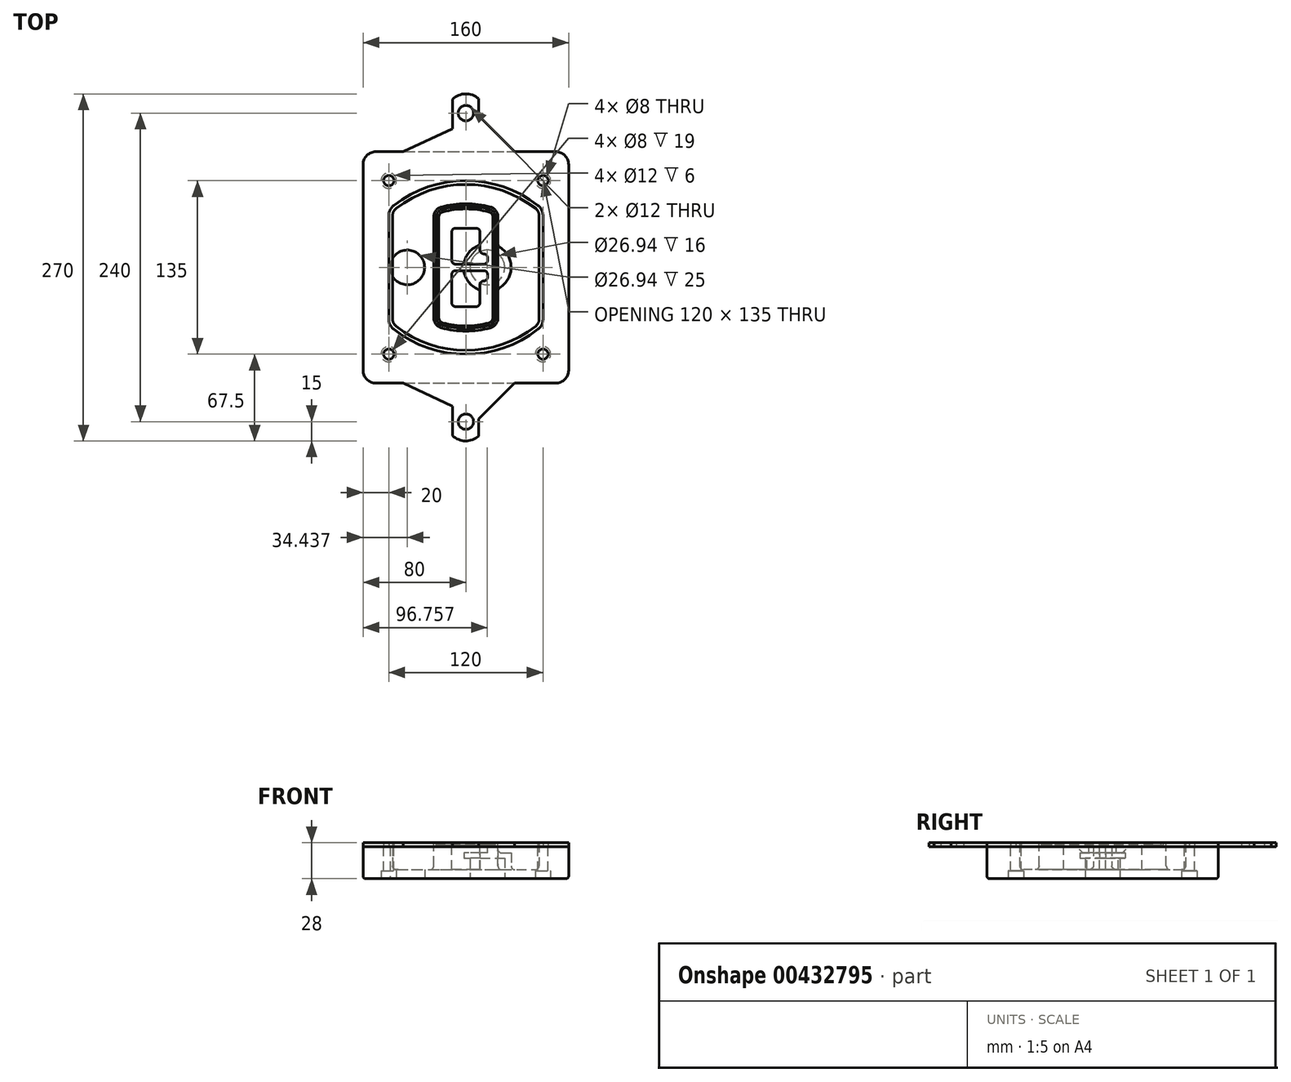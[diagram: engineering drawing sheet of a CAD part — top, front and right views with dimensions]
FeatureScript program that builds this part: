
annotation { "Feature Type Name" : "Feature", "Feature Type Description" : "" }
export const myFeature = defineFeature(function(context is Context, id is Id, definition is map)
    precondition{}
    {
        {
            var Q0;
            Q0=qCreatedBy(makeId("Top.planeOp"),FACE);
            var sketch = newSketch(context, id + "F0", { "sketchPlane" : qUnion([Q0])});
            skPoint(sketch, "E0.rect.middle", {"position": v(0, 0) * mm});
            skLineSegment(sketch, "E1.bottom", {"start": v(-70, -90) * mm, "end": v(70, -90) * mm});
            skLineSegment(sketch, "E1.top", {"start": v(-70, 90) * mm, "end": v(70, 90) * mm});
            skLineSegment(sketch, "E1.left", {"start": v(-80, -80) * mm, "end": v(-80, 80) * mm});
            skLineSegment(sketch, "E1.right", {"start": v(80, -80) * mm, "end": v(80, 80) * mm});
            skLineSegment(sketch, "E2", {"start": v(-80, 90) * mm, "end": v(80, -90) * mm, "construction": true});
            skLineSegment(sketch, "E3", {"start": v(80, 90) * mm, "end": v(-80, -90) * mm, "construction": true});
            skCircle(sketch, "E4", {"center": v(-60, 67.5) * mm, "radius": 4 * mm});
            skCircle(sketch, "E5", {"center": v(60, 67.5) * mm, "radius": 4 * mm});
            skCircle(sketch, "E6", {"center": v(60, -67.5) * mm, "radius": 4 * mm});
            skCircle(sketch, "E7", {"center": v(-60, -67.5) * mm, "radius": 4 * mm});
            skLineSegment(sketch, "E8", {"start": v(-60, 67.5) * mm, "end": v(60, 67.5) * mm, "construction": true});
            skLineSegment(sketch, "E9", {"start": v(60, 67.5) * mm, "end": v(60, -67.5) * mm, "construction": true});
            skLineSegment(sketch, "E10", {"start": v(60, -67.5) * mm, "end": v(-60, -67.5) * mm, "construction": true});
            skLineSegment(sketch, "E11", {"start": v(-60, -67.5) * mm, "end": v(-60, 67.5) * mm, "construction": true});
            skLineSegment(sketch, "E12", {"start": v(-60, 40.3) * mm, "end": v(-60, -40.3) * mm});
            skLineSegment(sketch, "E13", {"start": v(60, 40.3) * mm, "end": v(60, -40.3) * mm});
            skArc(sketch, "E14", {"start": v(56.15, 48.18) * mm, "mid": v(0, 67.5) * mm, "end": v(-56.15, 48.18) * mm});
            skArc(sketch, "E15", {"start": v(-56.15, -48.18) * mm, "mid": v(0, -67.5) * mm, "end": v(56.15, -48.18) * mm});
            skLineSegment(sketch, "E16", {"start": v(-60, 0) * mm, "end": v(60, 0) * mm, "construction": true});
            skPoint(sketch, "E17.visualSharp", {"position": v(-60, -45) * mm});
            skArc(sketch, "E17.filletArc", {"start": v(-60, -40.3) * mm, "mid": v(-58.99, -44.68) * mm, "end": v(-56.15, -48.18) * mm});
            skPoint(sketch, "E18.visualSharp", {"position": v(-60, 45) * mm});
            skArc(sketch, "E18.filletArc", {"start": v(-56.15, 48.18) * mm, "mid": v(-58.99, 44.68) * mm, "end": v(-60, 40.3) * mm});
            skPoint(sketch, "E19.visualSharp", {"position": v(60, 45) * mm});
            skArc(sketch, "E19.filletArc", {"start": v(60, 40.3) * mm, "mid": v(58.99, 44.68) * mm, "end": v(56.15, 48.18) * mm});
            skPoint(sketch, "E20.visualSharp", {"position": v(60, -45) * mm});
            skArc(sketch, "E20.filletArc", {"start": v(56.15, -48.18) * mm, "mid": v(58.99, -44.68) * mm, "end": v(60, -40.3) * mm});
            skPoint(sketch, "E21.visualSharp", {"position": v(-80, 90) * mm});
            skArc(sketch, "E21.filletArc", {"start": v(-70, 90) * mm, "mid": v(-77.07, 87.07) * mm, "end": v(-80, 80) * mm});
            skPoint(sketch, "E22.visualSharp", {"position": v(80, 90) * mm});
            skArc(sketch, "E22.filletArc", {"start": v(80, 80) * mm, "mid": v(77.07, 87.07) * mm, "end": v(70, 90) * mm});
            skPoint(sketch, "E23.visualSharp", {"position": v(80, -90) * mm});
            skArc(sketch, "E23.filletArc", {"start": v(70, -90) * mm, "mid": v(77.07, -87.07) * mm, "end": v(80, -80) * mm});
            skPoint(sketch, "E24.visualSharp", {"position": v(-80, -90) * mm});
            skArc(sketch, "E24.filletArc", {"start": v(-80, -80) * mm, "mid": v(-77.07, -87.07) * mm, "end": v(-70, -90) * mm});
            skArc(sketch, "E25.0", {"start": v(57, 40.3) * mm, "mid": v(56.3, 43.36) * mm, "end": v(54.3, 45.81) * mm});
            skLineSegment(sketch, "E25.1", {"start": v(57, 40.3) * mm, "end": v(57, -40.3) * mm});
            skArc(sketch, "E25.2", {"start": v(54.3, -45.81) * mm, "mid": v(56.3, -43.36) * mm, "end": v(57, -40.3) * mm});
            skArc(sketch, "E25.3", {"start": v(-54.3, -45.81) * mm, "mid": v(0, -64.5) * mm, "end": v(54.3, -45.81) * mm});
            skArc(sketch, "E25.4", {"start": v(-57, -40.3) * mm, "mid": v(-56.3, -43.36) * mm, "end": v(-54.3, -45.81) * mm});
            skArc(sketch, "E25.5", {"start": v(54.3, 45.81) * mm, "mid": v(0, 64.5) * mm, "end": v(-54.3, 45.81) * mm});
            skLineSegment(sketch, "E25.6", {"start": v(-57, 40.3) * mm, "end": v(-57, -40.3) * mm});
            skArc(sketch, "E25.7", {"start": v(-54.3, 45.81) * mm, "mid": v(-56.3, 43.36) * mm, "end": v(-57, 40.3) * mm});
            skArc(sketch, "E26.0", {"start": v(-58.62, 51.33) * mm, "mid": v(-62.58, 46.43) * mm, "end": v(-64, 40.3) * mm});
            skArc(sketch, "E26.1", {"start": v(58.62, 51.33) * mm, "mid": v(0, 71.5) * mm, "end": v(-58.62, 51.33) * mm});
            skArc(sketch, "E26.2", {"start": v(64, 40.3) * mm, "mid": v(62.58, 46.43) * mm, "end": v(58.62, 51.33) * mm});
            skLineSegment(sketch, "E26.3", {"start": v(64, 40.3) * mm, "end": v(64, -40.3) * mm});
            skArc(sketch, "E26.4", {"start": v(58.62, -51.33) * mm, "mid": v(62.58, -46.43) * mm, "end": v(64, -40.3) * mm});
            skLineSegment(sketch, "E26.5", {"start": v(-64, 40.3) * mm, "end": v(-64, -40.3) * mm});
            skArc(sketch, "E26.6", {"start": v(-58.62, -51.33) * mm, "mid": v(0, -71.5) * mm, "end": v(58.62, -51.33) * mm});
            skArc(sketch, "E26.7", {"start": v(-64, -40.3) * mm, "mid": v(-62.58, -46.43) * mm, "end": v(-58.62, -51.33) * mm});
            skSolve(sketch);
        }
        {
            var Q0;
            Q0=makeQuery(id+"F0.imprint","IMPRINT",FACE,{"disambiguationData":[TD([[makeQuery(id+"F0.imprint","IMPRINT",EDGE,{"derivedFrom":sQuery(id+"F0.wireOp",EDGE,"E1.bottom")}),1.0]])]});
            var Q1;
            Q1=makeQuery(id+"F0.imprint","IMPRINT",FACE,{"disambiguationData":[TD([[makeQuery(id+"F0.imprint","IMPRINT",EDGE,{"derivedFrom":sQuery(id+"F0.wireOp",EDGE,"E12")}),1.0]])]});
            var Q2;
            Q2=makeQuery(id+"F0.imprint","IMPRINT",FACE,{"disambiguationData":[TD([[makeQuery(id+"F0.imprint","IMPRINT",EDGE,{"derivedFrom":sQuery(id+"F0.wireOp",EDGE,"E25.0")}),1.0]])]});
            var Q3;
            Q3=makeQuery(id+"F0.imprint","IMPRINT",FACE,{"disambiguationData":[TD([[makeQuery(id+"F0.imprint","IMPRINT",EDGE,{"derivedFrom":sQuery(id+"F0.wireOp",EDGE,"E12")}),-1.0]])]});
            extrude(context, id + "F1", {"entities" : qUnion([Q0, Q1, Q2, Q3]), "oppositeDirection" : true, "depth" : 25 * mm});
        }
        {
            var Q0;
            Q0=makeQuery(id+"F0.imprint","IMPRINT",FACE,{"disambiguationData":[TD([[makeQuery(id+"F0.imprint","IMPRINT",EDGE,{"derivedFrom":sQuery(id+"F0.wireOp",EDGE,"E12")}),1.0]])]});
            extrude(context, id + "F2", {"entities" : qUnion([Q0]), "operationType" : NewBodyOperationType.ADD, "depth" : 3 * mm});
        }
        {
            var Q0;
            Q0=makeQuery(id+"F0.imprint","IMPRINT",FACE,{"disambiguationData":[TD([[makeQuery(id+"F0.imprint","IMPRINT",EDGE,{"derivedFrom":sQuery(id+"F0.wireOp",EDGE,"E25.0")}),1.0]])]});
            extrude(context, id + "F3", {"entities" : qUnion([Q0]), "operationType" : NewBodyOperationType.REMOVE, "oppositeDirection" : true, "depth" : 18 * mm});
        }
        {
            var Q0;
            Q0=makeQuery(id+"F2.opExtrude","CAP_FACE",FACE,{"disambiguationData":[OSD([sQuery(id+"F0.wireOp",EDGE,"E12"),sQuery(id+"F0.wireOp",EDGE,"E13"),sQuery(id+"F0.wireOp",EDGE,"E14"),sQuery(id+"F0.wireOp",EDGE,"E15"),sQuery(id+"F0.wireOp",EDGE,"E17.filletArc"),sQuery(id+"F0.wireOp",EDGE,"E18.filletArc"),sQuery(id+"F0.wireOp",EDGE,"E19.filletArc"),sQuery(id+"F0.wireOp",EDGE,"E20.filletArc"),sQuery(id+"F0.wireOp",EDGE,"E25.0"),sQuery(id+"F0.wireOp",EDGE,"E25.1"),sQuery(id+"F0.wireOp",EDGE,"E25.2"),sQuery(id+"F0.wireOp",EDGE,"E25.3"),sQuery(id+"F0.wireOp",EDGE,"E25.4"),sQuery(id+"F0.wireOp",EDGE,"E25.5"),sQuery(id+"F0.wireOp",EDGE,"E25.6"),sQuery(id+"F0.wireOp",EDGE,"E25.7")])],"isStart":false});
            var sketch = newSketch(context, id + "F4", { "sketchPlane" : qUnion([Q0])});
            skArc(sketch, "E27.0", {"start": v(-19.08, -46.97) * mm, "mid": v(0, -49.5) * mm, "end": v(19.08, -46.97) * mm});
            skArc(sketch, "E28.0", {"start": v(19.08, 46.97) * mm, "mid": v(0, 49.5) * mm, "end": v(-19.08, 46.97) * mm});
            skLineSegment(sketch, "E29", {"start": v(-25, 39.25) * mm, "end": v(-25, -39.25) * mm});
            skLineSegment(sketch, "E30", {"start": v(25, 39.25) * mm, "end": v(25, -39.25) * mm});
            skLineSegment(sketch, "E31", {"start": v(-25, 45.1) * mm, "end": v(25, 45.1) * mm, "construction": true});
            skLineSegment(sketch, "E32", {"start": v(-25, -45.1) * mm, "end": v(25, -45.1) * mm, "construction": true});
            skPoint(sketch, "E33.visualSharp", {"position": v(-25, 45.1) * mm});
            skArc(sketch, "E33.filletArc", {"start": v(-19.08, 46.97) * mm, "mid": v(-23.35, 44.11) * mm, "end": v(-25, 39.25) * mm});
            skPoint(sketch, "E34.visualSharp", {"position": v(25, 45.1) * mm});
            skArc(sketch, "E34.filletArc", {"start": v(25, 39.25) * mm, "mid": v(23.35, 44.11) * mm, "end": v(19.08, 46.97) * mm});
            skPoint(sketch, "E35.visualSharp", {"position": v(25, -45.1) * mm});
            skArc(sketch, "E35.filletArc", {"start": v(19.08, -46.97) * mm, "mid": v(23.35, -44.11) * mm, "end": v(25, -39.25) * mm});
            skPoint(sketch, "E36.visualSharp", {"position": v(-25, -45.1) * mm});
            skArc(sketch, "E36.filletArc", {"start": v(-25, -39.25) * mm, "mid": v(-23.35, -44.11) * mm, "end": v(-19.08, -46.97) * mm});
            skArc(sketch, "E37.0", {"start": v(54.3, 45.81) * mm, "mid": v(0, 64.5) * mm, "end": v(-54.3, 45.81) * mm});
            skArc(sketch, "E37.1", {"start": v(-54.3, 45.81) * mm, "mid": v(-56.3, 43.36) * mm, "end": v(-57, 40.3) * mm});
            skLineSegment(sketch, "E37.2", {"start": v(-57, 40.3) * mm, "end": v(-57, -40.3) * mm});
            skArc(sketch, "E37.3", {"start": v(-57, -40.3) * mm, "mid": v(-56.3, -43.36) * mm, "end": v(-54.3, -45.81) * mm});
            skArc(sketch, "E37.4", {"start": v(-54.3, -45.81) * mm, "mid": v(0, -64.5) * mm, "end": v(54.3, -45.81) * mm});
            skArc(sketch, "E37.5", {"start": v(54.3, -45.81) * mm, "mid": v(56.3, -43.36) * mm, "end": v(57, -40.3) * mm});
            skLineSegment(sketch, "E37.6", {"start": v(57, 40.3) * mm, "end": v(57, -40.3) * mm});
            skArc(sketch, "E37.7", {"start": v(57, 40.3) * mm, "mid": v(56.3, 43.36) * mm, "end": v(54.3, 45.81) * mm});
            skLineSegment(sketch, "E38.0", {"start": v(23, 39.25) * mm, "end": v(23, -39.25) * mm});
            skArc(sketch, "E38.1", {"start": v(18.56, -45.04) * mm, "mid": v(21.76, -42.9) * mm, "end": v(23, -39.25) * mm});
            skArc(sketch, "E38.2", {"start": v(-18.56, -45.04) * mm, "mid": v(0, -47.5) * mm, "end": v(18.56, -45.04) * mm});
            skArc(sketch, "E38.3", {"start": v(-23, -39.25) * mm, "mid": v(-21.76, -42.9) * mm, "end": v(-18.56, -45.04) * mm});
            skLineSegment(sketch, "E38.4", {"start": v(-23, 39.25) * mm, "end": v(-23, -39.25) * mm});
            skArc(sketch, "E38.5", {"start": v(23, 39.25) * mm, "mid": v(21.76, 42.9) * mm, "end": v(18.56, 45.04) * mm});
            skArc(sketch, "E38.6", {"start": v(-18.56, 45.04) * mm, "mid": v(-21.76, 42.9) * mm, "end": v(-23, 39.25) * mm});
            skArc(sketch, "E38.7", {"start": v(18.56, 45.04) * mm, "mid": v(0, 47.5) * mm, "end": v(-18.56, 45.04) * mm});
            skArc(sketch, "E39.0", {"start": v(21, 39.25) * mm, "mid": v(20.18, 41.68) * mm, "end": v(18.04, 43.1) * mm});
            skLineSegment(sketch, "E39.1", {"start": v(21, 39.25) * mm, "end": v(21, -39.25) * mm});
            skArc(sketch, "E39.2", {"start": v(18.04, -43.1) * mm, "mid": v(20.18, -41.68) * mm, "end": v(21, -39.25) * mm});
            skArc(sketch, "E39.3", {"start": v(-18.04, -43.1) * mm, "mid": v(0, -45.5) * mm, "end": v(18.04, -43.1) * mm});
            skArc(sketch, "E39.4", {"start": v(-21, -39.25) * mm, "mid": v(-20.18, -41.68) * mm, "end": v(-18.04, -43.1) * mm});
            skArc(sketch, "E39.5", {"start": v(18.04, 43.1) * mm, "mid": v(0, 45.5) * mm, "end": v(-18.04, 43.1) * mm});
            skLineSegment(sketch, "E39.6", {"start": v(-21, 39.25) * mm, "end": v(-21, -39.25) * mm});
            skArc(sketch, "E39.7", {"start": v(-18.04, 43.1) * mm, "mid": v(-20.18, 41.68) * mm, "end": v(-21, 39.25) * mm});
            skLineSegment(sketch, "E40", {"start": v(-25, 0) * mm, "end": v(25, 0) * mm, "construction": true});
            skLineSegment(sketch, "E41", {"start": v(-11, 5.5) * mm, "end": v(-11, 27.5) * mm});
            skLineSegment(sketch, "E42", {"start": v(-8, 30.5) * mm, "end": v(8, 30.5) * mm});
            skLineSegment(sketch, "E43", {"start": v(11, 27.5) * mm, "end": v(11, 13.5) * mm});
            skLineSegment(sketch, "E44", {"start": v(14, 10.5) * mm, "end": v(14, 10.5) * mm});
            skLineSegment(sketch, "E45", {"start": v(17, 7.5) * mm, "end": v(17, 5.5) * mm});
            skLineSegment(sketch, "E46", {"start": v(14, 2.5) * mm, "end": v(-8, 2.5) * mm});
            skPoint(sketch, "E47.visualSharp", {"position": v(-11, 30.5) * mm});
            skArc(sketch, "E47.filletArc", {"start": v(-8, 30.5) * mm, "mid": v(-10.12, 29.62) * mm, "end": v(-11, 27.5) * mm});
            skPoint(sketch, "E48.visualSharp", {"position": v(11, 30.5) * mm});
            skArc(sketch, "E48.filletArc", {"start": v(11, 27.5) * mm, "mid": v(10.12, 29.62) * mm, "end": v(8, 30.5) * mm});
            skPoint(sketch, "E49.visualSharp", {"position": v(11, 10.5) * mm});
            skArc(sketch, "E49.filletArc", {"start": v(11, 13.5) * mm, "mid": v(11.88, 11.38) * mm, "end": v(14, 10.5) * mm});
            skPoint(sketch, "E50.visualSharp", {"position": v(17, 10.5) * mm});
            skArc(sketch, "E50.filletArc", {"start": v(17, 7.5) * mm, "mid": v(16.12, 9.62) * mm, "end": v(14, 10.5) * mm});
            skPoint(sketch, "E51.visualSharp", {"position": v(17, 2.5) * mm});
            skArc(sketch, "E51.filletArc", {"start": v(14, 2.5) * mm, "mid": v(16.12, 3.38) * mm, "end": v(17, 5.5) * mm});
            skPoint(sketch, "E52.visualSharp", {"position": v(-11, 2.5) * mm});
            skArc(sketch, "E52.filletArc", {"start": v(-11, 5.5) * mm, "mid": v(-10.12, 3.38) * mm, "end": v(-8, 2.5) * mm});
            skLineSegment(sketch, "E53.0.MirrorCS", {"start": v(14, -2.5) * mm, "end": v(-8, -2.5) * mm});
            skArc(sketch, "E54.0.MirrorCS", {"start": v(-11, -5.5) * mm, "mid": v(-10.12, -3.38) * mm, "end": v(-8, -2.5) * mm});
            skLineSegment(sketch, "E55.0.MirrorCS", {"start": v(-11, -5.5) * mm, "end": v(-11, -27.5) * mm});
            skArc(sketch, "E56.0.MirrorCS", {"start": v(-8, -30.5) * mm, "mid": v(-10.12, -29.62) * mm, "end": v(-11, -27.5) * mm});
            skLineSegment(sketch, "E57.0.MirrorCS", {"start": v(-8, -30.5) * mm, "end": v(8, -30.5) * mm});
            skArc(sketch, "E58.0.MirrorCS", {"start": v(11, -27.5) * mm, "mid": v(10.12, -29.62) * mm, "end": v(8, -30.5) * mm});
            skLineSegment(sketch, "E59.0.MirrorCS", {"start": v(11, -27.5) * mm, "end": v(11, -13.5) * mm});
            skArc(sketch, "E60.0.MirrorCS", {"start": v(11, -13.5) * mm, "mid": v(11.88, -11.38) * mm, "end": v(14, -10.5) * mm});
            skArc(sketch, "E61.0.MirrorCS", {"start": v(17, -7.5) * mm, "mid": v(16.12, -9.62) * mm, "end": v(14, -10.5) * mm});
            skLineSegment(sketch, "E62.0.MirrorCS", {"start": v(17, -7.5) * mm, "end": v(17, -5.5) * mm});
            skArc(sketch, "E63.0.MirrorCS", {"start": v(14, -2.5) * mm, "mid": v(16.12, -3.38) * mm, "end": v(17, -5.5) * mm});
            skSolve(sketch);
        }
        {
            var Q0;
            Q0=makeQuery(id+"F4.imprint","IMPRINT",FACE,{"disambiguationData":[TD([[makeQuery(id+"F4.imprint","IMPRINT",EDGE,{"derivedFrom":sQuery(id+"F4.wireOp",EDGE,"E27.0")}),1.0]])]});
            var Q1;
            Q1=makeQuery(id+"F4.imprint","IMPRINT",FACE,{"disambiguationData":[TD([[makeQuery(id+"F4.imprint","IMPRINT",EDGE,{"derivedFrom":sQuery(id+"F4.wireOp",EDGE,"E38.0")}),-1.0]])]});
            var Q2;
            Q2=makeQuery(id+"F4.imprint","IMPRINT",FACE,{"disambiguationData":[TD([[makeQuery(id+"F4.imprint","IMPRINT",EDGE,{"derivedFrom":sQuery(id+"F4.wireOp",EDGE,"E39.0")}),1.0]])]});
            extrude(context, id + "F5", {"entities" : qUnion([Q0, Q1, Q2]), "operationType" : NewBodyOperationType.ADD, "endBound" : BoundingType.UP_TO_NEXT, "oppositeDirection" : true, "depth" : 25 * mm});
        }
        {
            var Q0;
            Q0=makeQuery(id+"F4.imprint","IMPRINT",FACE,{"disambiguationData":[TD([[makeQuery(id+"F4.imprint","IMPRINT",EDGE,{"derivedFrom":sQuery(id+"F4.wireOp",EDGE,"E38.0")}),-1.0]])]});
            extrude(context, id + "F6", {"entities" : qUnion([Q0]), "operationType" : NewBodyOperationType.REMOVE, "oppositeDirection" : true, "depth" : 2 * mm});
        }
        {
            var Q0;
            Q0=makeQuery(id+"F1.opExtrude","CAP_FACE",FACE,{"disambiguationData":[OSD([sQuery(id+"F0.wireOp",EDGE,"E1.bottom"),sQuery(id+"F0.wireOp",EDGE,"E1.top"),sQuery(id+"F0.wireOp",EDGE,"E1.left"),sQuery(id+"F0.wireOp",EDGE,"E1.right"),sQuery(id+"F0.wireOp",EDGE,"E4"),sQuery(id+"F0.wireOp",EDGE,"E5"),sQuery(id+"F0.wireOp",EDGE,"E6"),sQuery(id+"F0.wireOp",EDGE,"E7"),sQuery(id+"F0.wireOp",EDGE,"E21.filletArc"),sQuery(id+"F0.wireOp",EDGE,"E22.filletArc"),sQuery(id+"F0.wireOp",EDGE,"E23.filletArc"),sQuery(id+"F0.wireOp",EDGE,"E24.filletArc")])],"isStart":false});
            var sketch = newSketch(context, id + "F7", { "sketchPlane" : qUnion([Q0])});
            skCircle(sketch, "E64", {"center": v(16.76, 0) * mm, "radius": 13.47 * mm});
            skCircle(sketch, "E65", {"center": v(-45.56, 0) * mm, "radius": 13.47 * mm});
            skLineSegment(sketch, "E66", {"start": v(80, 0) * mm, "end": v(-80, 0) * mm});
            skCircle(sketch, "E67", {"center": v(16.76, 0) * mm, "radius": 18.47 * mm});
            skCircle(sketch, "E68", {"center": v(60, -67.5) * mm, "radius": 6 * mm});
            skCircle(sketch, "E69", {"center": v(-60, -67.5) * mm, "radius": 6 * mm});
            skCircle(sketch, "E70", {"center": v(-60, 67.5) * mm, "radius": 6 * mm});
            skCircle(sketch, "E71", {"center": v(60, 67.5) * mm, "radius": 6 * mm});
            skSolve(sketch);
        }
        {
            var Q0;
            {var subQ1=sQuery(id+"F7.wireOp",EDGE,"E66");var subQ4=sQuery(id+"F7.wireOp",EDGE,"E64");var subQ6=makeQuery(id+"F7.imprint","INTERSECT",VERTEX,{"disambiguationData":[OD(0.0)],"derivedFrom":[subQ4,subQ1]});Q0=makeQuery(id+"F7.imprint","IMPRINT",FACE,{"disambiguationData":[TD([[makeQuery(id+"F7.imprint","IMPRINT",EDGE,{"disambiguationData":[TD([[subQ6,-1.0]])],"derivedFrom":subQ4}),-1.0]])]});}
            var Q1;
            {var subQ0=sQuery(id+"F7.wireOp",EDGE,"E66");var subQ1=sQuery(id+"F7.wireOp",EDGE,"E64");var subQ3=makeQuery(id+"F7.imprint","INTERSECT",VERTEX,{"disambiguationData":[OD(0.0)],"derivedFrom":[subQ1,subQ0]});Q1=makeQuery(id+"F7.imprint","IMPRINT",FACE,{"disambiguationData":[TD([[makeQuery(id+"F7.imprint","IMPRINT",EDGE,{"disambiguationData":[TD([[subQ3,-1.0]])],"derivedFrom":subQ1}),1.0]])]});}
            var Q2;
            {var subQ0=sQuery(id+"F7.wireOp",EDGE,"E66");var subQ1=sQuery(id+"F7.wireOp",EDGE,"E64");var subQ3=makeQuery(id+"F7.imprint","INTERSECT",VERTEX,{"disambiguationData":[OD(0.0)],"derivedFrom":[subQ1,subQ0]});Q2=makeQuery(id+"F7.imprint","IMPRINT",FACE,{"disambiguationData":[TD([[makeQuery(id+"F7.imprint","IMPRINT",EDGE,{"disambiguationData":[TD([[subQ3,1.0]])],"derivedFrom":subQ1}),1.0]])]});}
            var Q3;
            {var subQ1=sQuery(id+"F7.wireOp",EDGE,"E66");var subQ4=sQuery(id+"F7.wireOp",EDGE,"E64");var subQ6=makeQuery(id+"F7.imprint","INTERSECT",VERTEX,{"disambiguationData":[OD(0.0)],"derivedFrom":[subQ4,subQ1]});Q3=makeQuery(id+"F7.imprint","IMPRINT",FACE,{"disambiguationData":[TD([[makeQuery(id+"F7.imprint","IMPRINT",EDGE,{"disambiguationData":[TD([[subQ6,1.0]])],"derivedFrom":subQ4}),-1.0]])]});}
            extrude(context, id + "F8", {"entities" : qUnion([Q0, Q1, Q2, Q3]), "operationType" : NewBodyOperationType.ADD, "oppositeDirection" : true, "depth" : 20 * mm});
        }
        {
            var Q0;
            {var subQ0=sQuery(id+"F7.wireOp",EDGE,"E66");var subQ1=sQuery(id+"F7.wireOp",EDGE,"E64");var subQ3=makeQuery(id+"F7.imprint","INTERSECT",VERTEX,{"disambiguationData":[OD(0.0)],"derivedFrom":[subQ1,subQ0]});Q0=makeQuery(id+"F7.imprint","IMPRINT",FACE,{"disambiguationData":[TD([[makeQuery(id+"F7.imprint","IMPRINT",EDGE,{"disambiguationData":[TD([[subQ3,-1.0]])],"derivedFrom":subQ1}),1.0]])]});}
            var Q1;
            {var subQ0=sQuery(id+"F7.wireOp",EDGE,"E66");var subQ1=sQuery(id+"F7.wireOp",EDGE,"E64");var subQ3=makeQuery(id+"F7.imprint","INTERSECT",VERTEX,{"disambiguationData":[OD(0.0)],"derivedFrom":[subQ1,subQ0]});Q1=makeQuery(id+"F7.imprint","IMPRINT",FACE,{"disambiguationData":[TD([[makeQuery(id+"F7.imprint","IMPRINT",EDGE,{"disambiguationData":[TD([[subQ3,1.0]])],"derivedFrom":subQ1}),1.0]])]});}
            extrude(context, id + "F9", {"entities" : qUnion([Q0, Q1]), "operationType" : NewBodyOperationType.REMOVE, "oppositeDirection" : true, "depth" : 16 * mm});
        }
        {
            var Q0;
            {var subQ0=sQuery(id+"F7.wireOp",EDGE,"E66");var subQ1=sQuery(id+"F7.wireOp",EDGE,"E65");var subQ3=makeQuery(id+"F7.imprint","INTERSECT",VERTEX,{"disambiguationData":[OD(0.0)],"derivedFrom":[subQ1,subQ0]});Q0=makeQuery(id+"F7.imprint","IMPRINT",FACE,{"disambiguationData":[TD([[makeQuery(id+"F7.imprint","IMPRINT",EDGE,{"disambiguationData":[TD([[subQ3,-1.0]])],"derivedFrom":subQ1}),1.0]])]});}
            var Q1;
            {var subQ0=sQuery(id+"F7.wireOp",EDGE,"E66");var subQ1=sQuery(id+"F7.wireOp",EDGE,"E65");var subQ3=makeQuery(id+"F7.imprint","INTERSECT",VERTEX,{"disambiguationData":[OD(0.0)],"derivedFrom":[subQ1,subQ0]});Q1=makeQuery(id+"F7.imprint","IMPRINT",FACE,{"disambiguationData":[TD([[makeQuery(id+"F7.imprint","IMPRINT",EDGE,{"disambiguationData":[TD([[subQ3,1.0]])],"derivedFrom":subQ1}),1.0]])]});}
            extrude(context, id + "F10", {"entities" : qUnion([Q0, Q1]), "operationType" : NewBodyOperationType.REMOVE, "oppositeDirection" : true, "depth" : 25 * mm});
        }
        {
            var Q0;
            Q0=makeQuery(id+"F7.imprint","IMPRINT",FACE,{"disambiguationData":[TD([[makeQuery(id+"F7.imprint","IMPRINT",EDGE,{"derivedFrom":sQuery(id+"F7.wireOp",EDGE,"E68")}),1.0]])]});
            var Q1;
            Q1=makeQuery(id+"F7.imprint","IMPRINT",FACE,{"disambiguationData":[TD([[makeQuery(id+"F7.imprint","IMPRINT",EDGE,{"derivedFrom":makeQuery(id+"F1.opExtrude","CAP_EDGE",EDGE,{"disambiguationData":[OSD([sQuery(id+"F0.wireOp",EDGE,"E5")])],"isStart":false})}),-1.0]])]});
            var Q2;
            Q2=makeQuery(id+"F7.imprint","IMPRINT",FACE,{"disambiguationData":[TD([[makeQuery(id+"F7.imprint","IMPRINT",EDGE,{"derivedFrom":sQuery(id+"F7.wireOp",EDGE,"E69")}),1.0]])]});
            var Q3;
            Q3=makeQuery(id+"F7.imprint","IMPRINT",FACE,{"disambiguationData":[TD([[makeQuery(id+"F7.imprint","IMPRINT",EDGE,{"derivedFrom":makeQuery(id+"F1.opExtrude","CAP_EDGE",EDGE,{"disambiguationData":[OSD([sQuery(id+"F0.wireOp",EDGE,"E4")])],"isStart":false})}),-1.0]])]});
            var Q4;
            Q4=makeQuery(id+"F7.imprint","IMPRINT",FACE,{"disambiguationData":[TD([[makeQuery(id+"F7.imprint","IMPRINT",EDGE,{"derivedFrom":sQuery(id+"F7.wireOp",EDGE,"E70")}),1.0]])]});
            var Q5;
            Q5=makeQuery(id+"F7.imprint","IMPRINT",FACE,{"disambiguationData":[TD([[makeQuery(id+"F7.imprint","IMPRINT",EDGE,{"derivedFrom":makeQuery(id+"F1.opExtrude","CAP_EDGE",EDGE,{"disambiguationData":[OSD([sQuery(id+"F0.wireOp",EDGE,"E7")])],"isStart":false})}),-1.0]])]});
            var Q6;
            Q6=makeQuery(id+"F7.imprint","IMPRINT",FACE,{"disambiguationData":[TD([[makeQuery(id+"F7.imprint","IMPRINT",EDGE,{"derivedFrom":sQuery(id+"F7.wireOp",EDGE,"E71")}),1.0]])]});
            var Q7;
            Q7=makeQuery(id+"F7.imprint","IMPRINT",FACE,{"disambiguationData":[TD([[makeQuery(id+"F7.imprint","IMPRINT",EDGE,{"derivedFrom":makeQuery(id+"F1.opExtrude","CAP_EDGE",EDGE,{"disambiguationData":[OSD([sQuery(id+"F0.wireOp",EDGE,"E6")])],"isStart":false})}),-1.0]])]});
            extrude(context, id + "F11", {"entities" : qUnion([Q0, Q1, Q2, Q3, Q4, Q5, Q6, Q7]), "operationType" : NewBodyOperationType.REMOVE, "oppositeDirection" : true, "depth" : 6 * mm});
        }
        {
            var Q0;
            Q0=makeQuery(id+"F9.boolean.opBoolean","COPY",FACE,{"derivedFrom":makeQuery(id+"F9.opExtrude","CAP_FACE",FACE,{"disambiguationData":[OSD([sQuery(id+"F7.wireOp",EDGE,"E64")])],"isStart":false})});
            var sketch = newSketch(context, id + "F12", { "sketchPlane" : qUnion([Q0])});
            skArc(sketch, "E72.0", {"start": v(11, 17.55) * mm, "mid": v(2.57, 11.82) * mm, "end": v(-1.54, 2.5) * mm});
            skArc(sketch, "E72.1", {"start": v(-1.54, -2.5) * mm, "mid": v(2.57, -11.82) * mm, "end": v(11, -17.55) * mm});
            skLineSegment(sketch, "E73", {"start": v(-1.54, -2.5) * mm, "end": v(14, -2.5) * mm});
            skLineSegment(sketch, "E74.0", {"start": v(14, 2.5) * mm, "end": v(-1.54, 2.5) * mm});
            skArc(sketch, "E74.1", {"start": v(14, 2.5) * mm, "mid": v(16.12, 3.38) * mm, "end": v(17, 5.5) * mm});
            skLineSegment(sketch, "E74.2", {"start": v(17, 7.5) * mm, "end": v(17, 5.5) * mm});
            skArc(sketch, "E74.3", {"start": v(17, 7.5) * mm, "mid": v(16.12, 9.62) * mm, "end": v(14, 10.5) * mm});
            skArc(sketch, "E74.4", {"start": v(11, 13.5) * mm, "mid": v(11.88, 11.38) * mm, "end": v(14, 10.5) * mm});
            skLineSegment(sketch, "E74.5", {"start": v(11, 17.55) * mm, "end": v(11, 13.5) * mm});
            skLineSegment(sketch, "E74.7", {"start": v(14, -2.5) * mm, "end": v(-1.54, -2.5) * mm});
            skArc(sketch, "E74.8", {"start": v(14, -2.5) * mm, "mid": v(16.12, -3.38) * mm, "end": v(17, -5.5) * mm});
            skLineSegment(sketch, "E74.9", {"start": v(17, -7.5) * mm, "end": v(17, -5.5) * mm});
            skArc(sketch, "E74.10", {"start": v(17, -7.5) * mm, "mid": v(16.12, -9.62) * mm, "end": v(14, -10.5) * mm});
            skArc(sketch, "E74.11", {"start": v(11, -13.5) * mm, "mid": v(11.88, -11.38) * mm, "end": v(14, -10.5) * mm});
            skLineSegment(sketch, "E74.12", {"start": v(11, -17.55) * mm, "end": v(11, -13.5) * mm});
            skPoint(sketch, "E75.orphan", {"position": v(11, -27.5) * mm});
            skPoint(sketch, "E76.orphan", {"position": v(-8, -2.5) * mm});
            skPoint(sketch, "E77.orphan", {"position": v(-8, 2.5) * mm});
            skPoint(sketch, "E78.orphan", {"position": v(11, 27.5) * mm});
            skSolve(sketch);
        }
        {
            var Q0;
            {var subQ7=sQuery(id+"F12.wireOp",EDGE,"E72.0");var subQ14=sQuery(id+"F12.wireOp",EDGE,"E72.1");var subQ16=sQuery(id+"F12.wireOp",EDGE,"E74.1");var subQ18=sQuery(id+"F12.wireOp",EDGE,"E74.8");Q0=qUnion([makeQuery(id+"F12.imprint","IMPRINT",FACE,{"disambiguationData":[TD([[makeQuery(id+"F12.imprint","IMPRINT",EDGE,{"derivedFrom":subQ7}),1.0]])]}),makeQuery(id+"F12.imprint","IMPRINT",FACE,{"disambiguationData":[TD([[makeQuery(id+"F12.imprint","IMPRINT",EDGE,{"derivedFrom":subQ14}),1.0]])]}),makeQuery(id+"F12.imprint","IMPRINT",FACE,{"disambiguationData":[TD([[makeQuery(id+"F12.imprint","IMPRINT",EDGE,{"derivedFrom":subQ16}),1.0]])]}),makeQuery(id+"F12.imprint","IMPRINT",FACE,{"disambiguationData":[TD([[makeQuery(id+"F12.imprint","IMPRINT",EDGE,{"derivedFrom":subQ18}),-1.0]])]})]);}
            var Q1;
            Q1=makeQuery(id+"F5.boolean.opBoolean","SPLIT",FACE,{"disambiguationData":[TD([makeQuery(id+"F5.opExtrude","SWEPT_FACE",FACE,{"disambiguationData":[OSD([sQuery(id+"F4.wireOp",EDGE,"E41")])]})])],"derivedFrom":makeQuery(id+"F3.boolean.opBoolean","COPY",FACE,{"derivedFrom":makeQuery(id+"F3.opExtrude","CAP_FACE",FACE,{"disambiguationData":[OSD([sQuery(id+"F0.wireOp",EDGE,"E25.0"),sQuery(id+"F0.wireOp",EDGE,"E25.1"),sQuery(id+"F0.wireOp",EDGE,"E25.2"),sQuery(id+"F0.wireOp",EDGE,"E25.3"),sQuery(id+"F0.wireOp",EDGE,"E25.4"),sQuery(id+"F0.wireOp",EDGE,"E25.5"),sQuery(id+"F0.wireOp",EDGE,"E25.6"),sQuery(id+"F0.wireOp",EDGE,"E25.7")])],"isStart":false})})});
            extrude(context, id + "F13", {"entities" : qUnion([Q0]), "operationType" : NewBodyOperationType.REMOVE, "endBound" : BoundingType.UP_TO_SURFACE, "endBoundEntityFace" : qUnion([Q1]), "depth" : 25 * mm});
        }
        {
            var Q0;
            Q0=makeQuery(id+"F3.boolean.opBoolean","COPY",EDGE,{"derivedFrom":makeQuery(id+"F3.opExtrude","CAP_EDGE",EDGE,{"disambiguationData":[OSD([sQuery(id+"F0.wireOp",EDGE,"E25.6")])],"isStart":false})});
            var Q1;
            Q1=makeQuery(id+"F8.boolean.opBoolean","INTERSECT",EDGE,{"derivedFrom":[makeQuery(id+"F5.opExtrude","SWEPT_FACE",FACE,{"disambiguationData":[OSD([sQuery(id+"F4.wireOp",EDGE,"E30")])]}),makeQuery(id+"F8.opExtrude","CAP_FACE",FACE,{"disambiguationData":[OSD([sQuery(id+"F7.wireOp",EDGE,"E67")])],"isStart":false})]});
            var Q2;
            Q2=makeQuery(id+"F8.boolean.opBoolean","INTERSECT",EDGE,{"disambiguationData":[OD(1.0)],"derivedFrom":[makeQuery(id+"F5.opExtrude","SWEPT_FACE",FACE,{"disambiguationData":[OSD([sQuery(id+"F4.wireOp",EDGE,"E30")])]}),makeQuery(id+"F8.opExtrude","SWEPT_FACE",FACE,{"disambiguationData":[OSD([sQuery(id+"F7.wireOp",EDGE,"E67")])]})]});
            var Q3;
            {var subQ0=sQuery(id+"F4.wireOp",EDGE,"E30");Q3=makeQuery(id+"F8.boolean.opBoolean","SPLIT",EDGE,{"disambiguationData":[TD([makeQuery(id+"F5.opExtrude","SWEPT_FACE",FACE,{"disambiguationData":[OSD([sQuery(id+"F4.wireOp",EDGE,"E35.filletArc")])]})])],"derivedFrom":makeQuery(id+"F5.opExtrude","CAP_EDGE",EDGE,{"disambiguationData":[OSD([subQ0])],"isStart":false})});}
            var Q4;
            {var subQ0=sQuery(id+"F0.wireOp",EDGE,"E25.7");var subQ1=sQuery(id+"F0.wireOp",EDGE,"E25.1");var subQ2=sQuery(id+"F0.wireOp",EDGE,"E25.6");var subQ3=sQuery(id+"F0.wireOp",EDGE,"E25.5");var subQ4=sQuery(id+"F0.wireOp",EDGE,"E25.4");var subQ5=sQuery(id+"F0.wireOp",EDGE,"E25.0");var subQ6=sQuery(id+"F0.wireOp",EDGE,"E25.2");var subQ7=sQuery(id+"F0.wireOp",EDGE,"E25.3");Q4=makeQuery(id+"F8.boolean.opBoolean","INTERSECT",EDGE,{"derivedFrom":[makeQuery(id+"F5.boolean.opBoolean","SPLIT",FACE,{"disambiguationData":[TD([makeQuery(id+"F2.opExtrude","SWEPT_FACE",FACE,{"disambiguationData":[OSD([subQ5])]})])],"derivedFrom":makeQuery(id+"F3.boolean.opBoolean","COPY",FACE,{"derivedFrom":makeQuery(id+"F3.opExtrude","CAP_FACE",FACE,{"disambiguationData":[OSD([subQ5,subQ1,subQ6,subQ7,subQ4,subQ3,subQ2,subQ0])],"isStart":false})})}),makeQuery(id+"F8.opExtrude","SWEPT_FACE",FACE,{"disambiguationData":[OSD([sQuery(id+"F7.wireOp",EDGE,"E67")])]})]});}
            var Q5;
            Q5=makeQuery(id+"F8.boolean.opBoolean","INTERSECT",EDGE,{"disambiguationData":[OD(0.0)],"derivedFrom":[makeQuery(id+"F5.opExtrude","SWEPT_FACE",FACE,{"disambiguationData":[OSD([sQuery(id+"F4.wireOp",EDGE,"E30")])]}),makeQuery(id+"F8.opExtrude","SWEPT_FACE",FACE,{"disambiguationData":[OSD([sQuery(id+"F7.wireOp",EDGE,"E67")])]})]});
            fillet(context, id + "F14", {"entities" : qUnion([Q0, Q1, Q2, Q3, Q4, Q5]), "radius" : 3 * mm, "tangentPropagation" : true, "allowEdgeOverflow" : false});
        }
        {
            var Q0;
            Q0=makeQuery(id+"F1.opExtrude","CAP_EDGE",EDGE,{"disambiguationData":[OSD([sQuery(id+"F0.wireOp",EDGE,"E1.bottom")])],"isStart":false});
            fillet(context, id + "F15", {"entities" : qUnion([Q0]), "radius" : 2 * mm, "tangentPropagation" : true, "allowEdgeOverflow" : false});
        }
        {
            var Q0;
            {var subQ0=sQuery(id+"F0.wireOp",EDGE,"E21.filletArc");var subQ1=sQuery(id+"F0.wireOp",EDGE,"E7");var subQ2=sQuery(id+"F0.wireOp",EDGE,"E6");var subQ3=sQuery(id+"F0.wireOp",EDGE,"E5");var subQ4=sQuery(id+"F0.wireOp",EDGE,"E4");var subQ5=sQuery(id+"F0.wireOp",EDGE,"E22.filletArc");var subQ6=sQuery(id+"F0.wireOp",EDGE,"E1.bottom");var subQ7=sQuery(id+"F0.wireOp",EDGE,"E1.right");var subQ8=sQuery(id+"F0.wireOp",EDGE,"E1.top");var subQ9=sQuery(id+"F0.wireOp",EDGE,"E1.left");var subQ10=sQuery(id+"F0.wireOp",EDGE,"E23.filletArc");var subQ11=sQuery(id+"F0.wireOp",EDGE,"E24.filletArc");Q0=makeQuery(id+"F2.boolean.opBoolean","SPLIT",FACE,{"disambiguationData":[TD([makeQuery(id+"F1.opExtrude","SWEPT_FACE",FACE,{"disambiguationData":[OSD([subQ6])]})])],"derivedFrom":makeQuery(id+"F1.opExtrude","CAP_FACE",FACE,{"disambiguationData":[OSD([subQ6,subQ8,subQ9,subQ7,subQ4,subQ3,subQ2,subQ1,subQ0,subQ5,subQ10,subQ11])],"isStart":true})});}
            var sketch = newSketch(context, id + "F16", { "sketchPlane" : qUnion([Q0])});
            skPoint(sketch, "E79", {"position": v(0, 90) * mm});
            skCircle(sketch, "E80", {"center": v(0, 120) * mm, "radius": 6 * mm});
            skLineSegment(sketch, "E81", {"start": v(0, 120) * mm, "end": v(0, 90) * mm, "construction": true});
            skArc(sketch, "E82", {"start": v(9.95, 131.23) * mm, "mid": v(-0.33, 135) * mm, "end": v(-10.43, 130.78) * mm});
            skLineSegment(sketch, "E83", {"start": v(-10.43, 130.78) * mm, "end": v(-10.43, 108) * mm});
            skLineSegment(sketch, "E84", {"start": v(-10.43, 108) * mm, "end": v(-48.67, 90) * mm});
            skLineSegment(sketch, "E85", {"start": v(9.95, 131.23) * mm, "end": v(9.95, 117.98) * mm});
            skLineSegment(sketch, "E86", {"start": v(9.95, 117.98) * mm, "end": v(37.92, 90) * mm});
            skLineSegment(sketch, "E87", {"start": v(-80, 0) * mm, "end": v(80, 0) * mm, "construction": true});
            skLineSegment(sketch, "E88.MirrorCS", {"start": v(-10.43, -130.78) * mm, "end": v(-10.43, -108) * mm});
            skLineSegment(sketch, "E89.MirrorCS", {"start": v(-10.43, -108) * mm, "end": v(-48.67, -90) * mm});
            skLineSegment(sketch, "E90.MirrorCS", {"start": v(0, -120) * mm, "end": v(0, -90) * mm, "construction": true});
            skCircle(sketch, "E91.MirrorC", {"center": v(0, -120) * mm, "radius": 6 * mm});
            skArc(sketch, "E92.MirrorCS", {"start": v(9.95, -131.23) * mm, "mid": v(-0.33, -135) * mm, "end": v(-10.43, -130.78) * mm});
            skLineSegment(sketch, "E93.MirrorCS", {"start": v(9.95, -131.23) * mm, "end": v(9.95, -117.98) * mm});
            skLineSegment(sketch, "E94.MirrorCS", {"start": v(9.95, -117.98) * mm, "end": v(37.92, -90) * mm});
            skSolve(sketch);
        }
        {
            var Q0;
            Q0=makeQuery(id+"F16.imprint","IMPRINT",FACE,{"disambiguationData":[TD([[makeQuery(id+"F16.imprint","IMPRINT",EDGE,{"derivedFrom":sQuery(id+"F16.wireOp",EDGE,"E80")}),-1.0]])]});
            var Q1;
            Q1=makeQuery(id+"F16.imprint","IMPRINT",FACE,{"disambiguationData":[TD([[makeQuery(id+"F16.imprint","IMPRINT",EDGE,{"derivedFrom":sQuery(id+"F16.wireOp",EDGE,"E88.MirrorCS")}),-1.0]])]});
            var Q2;
            Q2=makeQuery(id+"F16.imprint","IMPRINT",FACE,{"disambiguationData":[TD([[makeQuery(id+"F16.imprint","IMPRINT",EDGE,{"derivedFrom":makeQuery(id+"F1.opExtrude","CAP_EDGE",EDGE,{"disambiguationData":[OSD([sQuery(id+"F0.wireOp",EDGE,"E1.left")])],"isStart":true})}),-1.0]])]});
            var Q3;
            Q3=makeQuery(id+"F2.opExtrude","CAP_FACE",FACE,{"disambiguationData":[OSD([sQuery(id+"F0.wireOp",EDGE,"E12"),sQuery(id+"F0.wireOp",EDGE,"E13"),sQuery(id+"F0.wireOp",EDGE,"E14"),sQuery(id+"F0.wireOp",EDGE,"E15"),sQuery(id+"F0.wireOp",EDGE,"E17.filletArc"),sQuery(id+"F0.wireOp",EDGE,"E18.filletArc"),sQuery(id+"F0.wireOp",EDGE,"E19.filletArc"),sQuery(id+"F0.wireOp",EDGE,"E20.filletArc"),sQuery(id+"F0.wireOp",EDGE,"E25.0"),sQuery(id+"F0.wireOp",EDGE,"E25.1"),sQuery(id+"F0.wireOp",EDGE,"E25.2"),sQuery(id+"F0.wireOp",EDGE,"E25.3"),sQuery(id+"F0.wireOp",EDGE,"E25.4"),sQuery(id+"F0.wireOp",EDGE,"E25.5"),sQuery(id+"F0.wireOp",EDGE,"E25.6"),sQuery(id+"F0.wireOp",EDGE,"E25.7")])],"isStart":false});
            extrude(context, id + "F17", {"entities" : qUnion([Q0, Q1, Q2]), "endBound" : BoundingType.UP_TO_SURFACE, "endBoundEntityFace" : qUnion([Q3]), "depth" : 25 * mm});
        }
    });
